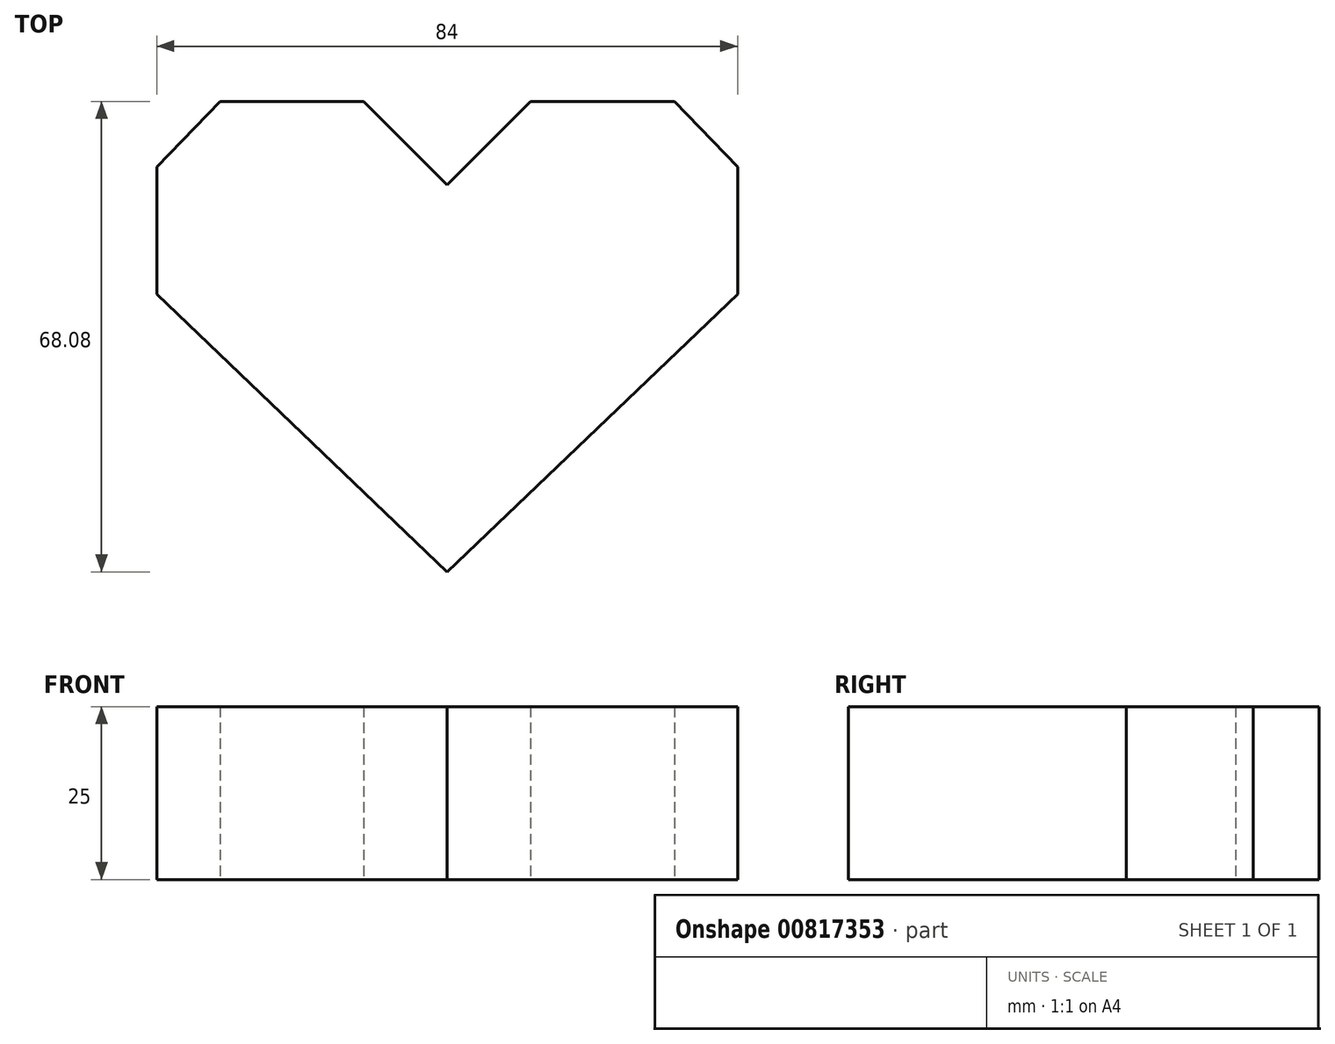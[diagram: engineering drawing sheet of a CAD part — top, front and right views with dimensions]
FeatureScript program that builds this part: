
annotation { "Feature Type Name" : "Feature", "Feature Type Description" : "" }
export const myFeature = defineFeature(function(context is Context, id is Id, definition is map)
    precondition{}
    {
        {
            var Q0;
            Q0=qCreatedBy(makeId("Top.planeOp"),FACE);
            var sketch = newSketch(context, id + "F0", { "sketchPlane" : qUnion([Q0])});
            skLineSegment(sketch, "E0.0", {"start": v(-42, -14.36) * mm, "end": v(-42, 3.99) * mm});
            skLineSegment(sketch, "E0.1", {"start": v(0, -54.58) * mm, "end": v(-42, -14.36) * mm});
            skLineSegment(sketch, "E0.2", {"start": v(-42, 3.99) * mm, "end": v(-32.87, 13.5) * mm});
            skLineSegment(sketch, "E0.3", {"start": v(0, -54.58) * mm, "end": v(42, -14.36) * mm});
            skLineSegment(sketch, "E0.4", {"start": v(42, -14.36) * mm, "end": v(42, 3.99) * mm});
            skLineSegment(sketch, "E0.5", {"start": v(42, 3.99) * mm, "end": v(32.87, 13.5) * mm});
            skLineSegment(sketch, "E0.6", {"start": v(-32.87, 13.5) * mm, "end": v(-12.07, 13.5) * mm});
            skLineSegment(sketch, "E0.7", {"start": v(-12.07, 13.5) * mm, "end": v(0, 1.43) * mm});
            skLineSegment(sketch, "E0.8", {"start": v(12.07, 13.5) * mm, "end": v(0, 1.43) * mm});
            skLineSegment(sketch, "E0.9", {"start": v(32.87, 13.5) * mm, "end": v(12.07, 13.5) * mm});
            skPoint(sketch, "E1.end.orphan", {"position": v(0, 8.5) * mm});
            skPoint(sketch, "E2.end.orphan", {"position": v(10, 18.5) * mm});
            skPoint(sketch, "E3.end.orphan", {"position": v(47, 6) * mm});
            skPoint(sketch, "E4.end.orphan", {"position": v(47, -16.5) * mm});
            skPoint(sketch, "E4.start.orphan", {"position": v(0, -61.5) * mm});
            skSolve(sketch);
        }
        {
            var Q0;
            Q0=makeQuery(id+"F0.imprint","IMPRINT",FACE,{"disambiguationData":[TD([[makeQuery(id+"F0.imprint","IMPRINT",EDGE,{"derivedFrom":sQuery(id+"F0.wireOp",EDGE,"E4")}),1.0]])]});
            var Q1;
            Q1=qSketchRegion(id+"F0",true);
            extrude(context, id + "F1", {"entities" : qUnion([Q0, Q1]), "depth" : 25 * mm, "offsetDistance" : 25 * mm});
        }
    });
